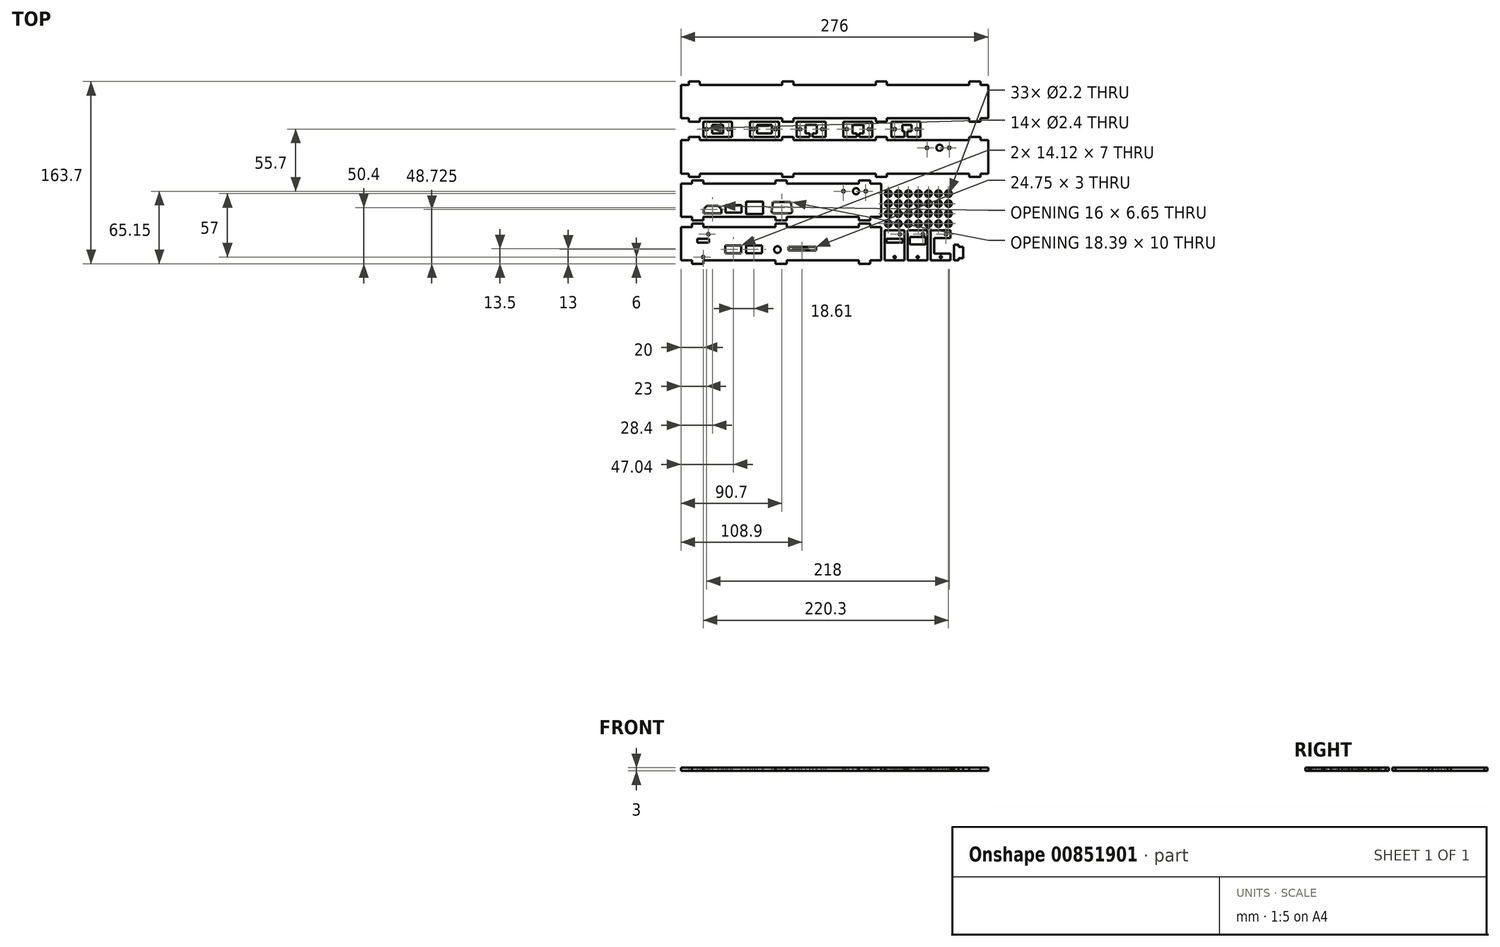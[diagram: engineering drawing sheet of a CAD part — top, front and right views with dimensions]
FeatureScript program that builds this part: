
annotation { "Feature Type Name" : "Feature", "Feature Type Description" : "" }
export const myFeature = defineFeature(function(context is Context, id is Id, definition is map)
    precondition{}
    {
        {
            var Q0;
            Q0=qCreatedBy(makeId("Top.planeOp"),FACE);
            var sketch = newSketch(context, id + "F0", { "sketchPlane" : qUnion([Q0])});
            skLineSegment(sketch, "E0.bottom", {"start": v(0, 0) * mm, "end": v(297, 0) * mm, "construction": true});
            skLineSegment(sketch, "E0.top", {"start": v(0, 210) * mm, "end": v(297, 210) * mm, "construction": true});
            skLineSegment(sketch, "E0.left", {"start": v(0, 0) * mm, "end": v(0, 210) * mm, "construction": true});
            skLineSegment(sketch, "E0.right", {"start": v(297, 0) * mm, "end": v(297, 210) * mm, "construction": true});
            skLineSegment(sketch, "E1.bottom", {"start": v(51, 132.7) * mm, "end": v(25, 132.7) * mm});
            skLineSegment(sketch, "E1.top", {"start": v(51, 119) * mm, "end": v(25, 119) * mm});
            skLineSegment(sketch, "E1.left", {"start": v(51, 132.7) * mm, "end": v(51, 119) * mm});
            skLineSegment(sketch, "E1.right", {"start": v(25, 132.7) * mm, "end": v(25, 119) * mm});
            skCircle(sketch, "E2", {"center": v(28, 125.85) * mm, "radius": 1.2 * mm});
            skCircle(sketch, "E3.MirrorC", {"center": v(48, 125.85) * mm, "radius": 1.2 * mm});
            skLineSegment(sketch, "E4.bottom", {"start": v(43, 129.7) * mm, "end": v(33, 129.7) * mm});
            skLineSegment(sketch, "E4.top", {"start": v(43, 122) * mm, "end": v(33, 122) * mm});
            skLineSegment(sketch, "E4.left", {"start": v(43, 129.7) * mm, "end": v(43, 122) * mm});
            skLineSegment(sketch, "E4.right", {"start": v(33, 129.7) * mm, "end": v(33, 122) * mm});
            skPoint(sketch, "E4.middle", {"position": v(38, 125.85) * mm});
            skLineSegment(sketch, "E5", {"start": v(95, 80) * mm, "end": v(95, 44) * mm, "construction": true});
            skLineSegment(sketch, "E6", {"start": v(143, 135.7) * mm, "end": v(143, 165.7) * mm, "construction": true});
            skLineSegment(sketch, "E7", {"start": v(95, 41) * mm, "end": v(95, 5) * mm, "construction": true});
            skLineSegment(sketch, "E8", {"start": v(25, 125.85) * mm, "end": v(51, 125.85) * mm, "construction": true});
            skLineSegment(sketch, "E9.bottom", {"start": v(93, 132.7) * mm, "end": v(67, 132.7) * mm});
            skLineSegment(sketch, "E9.top", {"start": v(93, 119) * mm, "end": v(67, 119) * mm});
            skLineSegment(sketch, "E9.left", {"start": v(93, 132.7) * mm, "end": v(93, 119) * mm});
            skLineSegment(sketch, "E9.right", {"start": v(67, 132.7) * mm, "end": v(67, 119) * mm});
            skCircle(sketch, "E10", {"center": v(70, 125.85) * mm, "radius": 1.2 * mm});
            skCircle(sketch, "E11.MirrorC", {"center": v(90, 125.85) * mm, "radius": 1.2 * mm});
            skLineSegment(sketch, "E12.bottom", {"start": v(86.65, 129.7) * mm, "end": v(73.35, 129.7) * mm});
            skLineSegment(sketch, "E12.top", {"start": v(86.65, 122) * mm, "end": v(73.35, 122) * mm});
            skLineSegment(sketch, "E12.left", {"start": v(86.65, 129.7) * mm, "end": v(86.65, 122) * mm});
            skLineSegment(sketch, "E12.right", {"start": v(73.35, 129.7) * mm, "end": v(73.35, 122) * mm});
            skPoint(sketch, "E12.middle", {"position": v(80, 125.85) * mm});
            skLineSegment(sketch, "E13", {"start": v(67, 125.85) * mm, "end": v(93, 125.85) * mm, "construction": true});
            skLineSegment(sketch, "E14.bottom", {"start": v(135, 132.7) * mm, "end": v(109, 132.7) * mm});
            skLineSegment(sketch, "E14.top", {"start": v(135, 119) * mm, "end": v(123.2, 119) * mm});
            skLineSegment(sketch, "E14.left", {"start": v(135, 132.7) * mm, "end": v(135, 119) * mm});
            skLineSegment(sketch, "E14.right", {"start": v(109, 132.7) * mm, "end": v(109, 119) * mm});
            skCircle(sketch, "E15", {"center": v(112, 125.85) * mm, "radius": 1.2 * mm});
            skCircle(sketch, "E16.MirrorC", {"center": v(132, 125.85) * mm, "radius": 1.2 * mm});
            skLineSegment(sketch, "E17.bottom", {"start": v(127, 129.7) * mm, "end": v(117, 129.7) * mm});
            skLineSegment(sketch, "E17.top", {"start": v(127, 122) * mm, "end": v(123.2, 122) * mm});
            skLineSegment(sketch, "E17.left", {"start": v(127, 129.7) * mm, "end": v(127, 122) * mm});
            skLineSegment(sketch, "E17.right", {"start": v(117, 129.7) * mm, "end": v(117, 122) * mm});
            skPoint(sketch, "E17.middle", {"position": v(122, 125.85) * mm});
            skLineSegment(sketch, "E18", {"start": v(109, 125.85) * mm, "end": v(135, 125.85) * mm, "construction": true});
            skLineSegment(sketch, "E19.bottom", {"start": v(220, 132.7) * mm, "end": v(194, 132.7) * mm});
            skLineSegment(sketch, "E19.top", {"start": v(220, 119) * mm, "end": v(208.2, 119) * mm});
            skLineSegment(sketch, "E19.left", {"start": v(220, 132.7) * mm, "end": v(220, 119) * mm});
            skLineSegment(sketch, "E19.right", {"start": v(194, 132.7) * mm, "end": v(194, 119) * mm});
            skCircle(sketch, "E20", {"center": v(197, 125.85) * mm, "radius": 1.2 * mm});
            skCircle(sketch, "E21.MirrorC", {"center": v(217, 125.85) * mm, "radius": 1.2 * mm});
            skLineSegment(sketch, "E22.top", {"start": v(212, 123.9) * mm, "end": v(208.2, 123.9) * mm});
            skPoint(sketch, "E22.middle", {"position": v(207, 125.85) * mm});
            skLineSegment(sketch, "E23", {"start": v(194, 125.85) * mm, "end": v(220, 125.85) * mm, "construction": true});
            skLineSegment(sketch, "E24", {"start": v(123.2, 122) * mm, "end": v(123.2, 119) * mm});
            skLineSegment(sketch, "E25", {"start": v(120.8, 122) * mm, "end": v(120.8, 119) * mm});
            skLineSegment(sketch, "E26", {"start": v(120.8, 122) * mm, "end": v(117, 122) * mm});
            skLineSegment(sketch, "E27", {"start": v(120.8, 119) * mm, "end": v(109, 119) * mm});
            skLineSegment(sketch, "E28", {"start": v(208.2, 123.9) * mm, "end": v(208.2, 119) * mm});
            skLineSegment(sketch, "E29", {"start": v(205.8, 123.9) * mm, "end": v(205.8, 119) * mm});
            skLineSegment(sketch, "E30", {"start": v(212, 123.9) * mm, "end": v(212, 129.7) * mm});
            skLineSegment(sketch, "E31", {"start": v(212, 129.7) * mm, "end": v(203.9, 129.7) * mm});
            skLineSegment(sketch, "E32", {"start": v(203.9, 129.7) * mm, "end": v(203.9, 123.9) * mm});
            skLineSegment(sketch, "E33", {"start": v(203.9, 123.9) * mm, "end": v(205.8, 123.9) * mm});
            skLineSegment(sketch, "E34", {"start": v(205.8, 119) * mm, "end": v(194, 119) * mm});
            skCircle(sketch, "E35", {"center": v(162.3, 70.15) * mm, "radius": 2.8 * mm});
            skCircle(sketch, "E36", {"center": v(171, 70.15) * mm, "radius": 1.2 * mm});
            skCircle(sketch, "E37", {"center": v(151, 70.15) * mm, "radius": 1.2 * mm});
            skLineSegment(sketch, "E38.bottom", {"start": v(177, 132.7) * mm, "end": v(151, 132.7) * mm});
            skLineSegment(sketch, "E38.top", {"start": v(177, 119) * mm, "end": v(165.2, 119) * mm});
            skLineSegment(sketch, "E38.left", {"start": v(177, 132.7) * mm, "end": v(177, 119) * mm});
            skLineSegment(sketch, "E38.right", {"start": v(151, 132.7) * mm, "end": v(151, 119) * mm});
            skCircle(sketch, "E39", {"center": v(154, 125.85) * mm, "radius": 1.2 * mm});
            skCircle(sketch, "E40.MirrorC", {"center": v(174, 125.85) * mm, "radius": 1.2 * mm});
            skLineSegment(sketch, "E41.bottom", {"start": v(169, 129.7) * mm, "end": v(159, 129.7) * mm});
            skLineSegment(sketch, "E41.top", {"start": v(169, 122) * mm, "end": v(165.2, 122) * mm});
            skLineSegment(sketch, "E41.left", {"start": v(169, 129.7) * mm, "end": v(169, 122) * mm});
            skLineSegment(sketch, "E41.right", {"start": v(159, 129.7) * mm, "end": v(159, 122) * mm});
            skPoint(sketch, "E41.middle", {"position": v(164, 125.85) * mm});
            skLineSegment(sketch, "E42", {"start": v(151, 125.85) * mm, "end": v(177, 125.85) * mm, "construction": true});
            skLineSegment(sketch, "E43", {"start": v(165.2, 122) * mm, "end": v(165.2, 119) * mm});
            skLineSegment(sketch, "E44", {"start": v(162.8, 122) * mm, "end": v(162.8, 119) * mm});
            skLineSegment(sketch, "E45", {"start": v(162.8, 122) * mm, "end": v(159, 122) * mm});
            skLineSegment(sketch, "E46", {"start": v(162.8, 119) * mm, "end": v(151, 119) * mm});
            skCircle(sketch, "E47", {"center": v(29.7, 31.5) * mm, "radius": 1.1 * mm});
            skCircle(sketch, "E48", {"center": v(25, 11) * mm, "radius": 1.1 * mm});
            skLineSegment(sketch, "E49", {"start": v(30.1, 24.1) * mm, "end": v(30.1, 27.3) * mm});
            skLineSegment(sketch, "E50", {"start": v(30.1, 27.3) * mm, "end": v(19.9, 27.3) * mm});
            skLineSegment(sketch, "E51", {"start": v(19.9, 27.3) * mm, "end": v(19.9, 24.1) * mm});
            skLineSegment(sketch, "E52", {"start": v(19.9, 24.1) * mm, "end": v(30.1, 24.1) * mm});
            skCircle(sketch, "E53", {"center": v(201.7, 31.5) * mm, "radius": 1.1 * mm});
            skCircle(sketch, "E54", {"center": v(197, 11) * mm, "radius": 1 * mm});
            skLineSegment(sketch, "E55", {"start": v(204.25, 24.1) * mm, "end": v(204.25, 27.3) * mm});
            skLineSegment(sketch, "E56", {"start": v(204.25, 27.3) * mm, "end": v(189.75, 27.3) * mm});
            skLineSegment(sketch, "E57", {"start": v(189.75, 27.3) * mm, "end": v(189.75, 24.1) * mm});
            skLineSegment(sketch, "E58", {"start": v(189.75, 24.1) * mm, "end": v(204.25, 24.1) * mm});
            skLineSegment(sketch, "E59", {"start": v(205.7, 8) * mm, "end": v(205.7, 35) * mm});
            skLineSegment(sketch, "E60", {"start": v(205.7, 35) * mm, "end": v(188, 35) * mm});
            skLineSegment(sketch, "E61", {"start": v(188, 35) * mm, "end": v(188, 8) * mm});
            skLineSegment(sketch, "E62", {"start": v(188, 8) * mm, "end": v(205.7, 8) * mm});
            skCircle(sketch, "E63", {"center": v(222.4, 31.5) * mm, "radius": 1.1 * mm});
            skCircle(sketch, "E64", {"center": v(217.7, 11) * mm, "radius": 1 * mm});
            skLineSegment(sketch, "E65", {"start": v(224.95, 22.45) * mm, "end": v(224.95, 28.95) * mm});
            skLineSegment(sketch, "E66", {"start": v(224.95, 28.95) * mm, "end": v(210.45, 28.95) * mm});
            skLineSegment(sketch, "E67", {"start": v(210.45, 28.95) * mm, "end": v(210.45, 22.45) * mm});
            skLineSegment(sketch, "E68", {"start": v(210.45, 22.45) * mm, "end": v(224.95, 22.45) * mm});
            skLineSegment(sketch, "E69", {"start": v(226.4, 8) * mm, "end": v(226.4, 35) * mm});
            skLineSegment(sketch, "E70", {"start": v(226.4, 35) * mm, "end": v(208.7, 35) * mm});
            skLineSegment(sketch, "E71", {"start": v(208.7, 35) * mm, "end": v(208.7, 8) * mm});
            skLineSegment(sketch, "E72", {"start": v(208.7, 8) * mm, "end": v(226.4, 8) * mm});
            skCircle(sketch, "E73", {"center": v(243.1, 31.5) * mm, "radius": 1.1 * mm});
            skCircle(sketch, "E74", {"center": v(238.4, 11) * mm, "radius": 1 * mm});
            skLineSegment(sketch, "E75", {"start": v(247.1, 28) * mm, "end": v(232.4, 28) * mm});
            skLineSegment(sketch, "E76", {"start": v(232.4, 28) * mm, "end": v(232.4, 14) * mm});
            skLineSegment(sketch, "E77", {"start": v(232.4, 14) * mm, "end": v(247.1, 14) * mm});
            skLineSegment(sketch, "E78", {"start": v(247.1, 8) * mm, "end": v(247.1, 14) * mm});
            skLineSegment(sketch, "E79", {"start": v(247.1, 35) * mm, "end": v(229.4, 35) * mm});
            skLineSegment(sketch, "E80", {"start": v(229.4, 35) * mm, "end": v(229.4, 8) * mm});
            skLineSegment(sketch, "E81", {"start": v(229.4, 8) * mm, "end": v(247.1, 8) * mm});
            skLineSegment(sketch, "E82", {"start": v(250.1, 22.2) * mm, "end": v(250.1, 8) * mm});
            skLineSegment(sketch, "E83", {"start": v(250.1, 8) * mm, "end": v(254.5, 8) * mm});
            skLineSegment(sketch, "E84", {"start": v(254.5, 8) * mm, "end": v(254.5, 10.1) * mm});
            skLineSegment(sketch, "E85", {"start": v(254.5, 10.1) * mm, "end": v(258.5, 10.1) * mm});
            skLineSegment(sketch, "E86", {"start": v(258.5, 10.1) * mm, "end": v(258.5, 20.1) * mm});
            skLineSegment(sketch, "E87", {"start": v(258.5, 20.1) * mm, "end": v(254.5, 20.1) * mm});
            skLineSegment(sketch, "E88", {"start": v(254.5, 20.1) * mm, "end": v(254.5, 22.2) * mm});
            skLineSegment(sketch, "E89", {"start": v(254.5, 22.2) * mm, "end": v(250.1, 22.2) * mm});
            skLineSegment(sketch, "E90", {"start": v(95.7, 51.4) * mm, "end": v(95.7, 59.4) * mm, "construction": true});
            skLineSegment(sketch, "E91", {"start": v(103.3, 52) * mm, "end": v(102.5, 58.8) * mm, "construction": true});
            skLineSegment(sketch, "E92.bottom", {"start": v(126.27, 17) * mm, "end": v(101.53, 17) * mm});
            skLineSegment(sketch, "E92.top", {"start": v(126.27, 20) * mm, "end": v(101.53, 20) * mm});
            skLineSegment(sketch, "E92.left", {"start": v(126.27, 17) * mm, "end": v(126.27, 20) * mm});
            skLineSegment(sketch, "E92.right", {"start": v(101.53, 17) * mm, "end": v(101.53, 20) * mm});
            skPoint(sketch, "E92.middle", {"position": v(113.9, 18.5) * mm});
            skCircle(sketch, "E93", {"center": v(91.7, 17.75) * mm, "radius": 2.5 * mm, "construction": true});
            skLineSegment(sketch, "E94.bottom", {"start": v(77.21, 21) * mm, "end": v(64.1, 21) * mm, "construction": true});
            skLineSegment(sketch, "E94.top", {"start": v(77.21, 15) * mm, "end": v(64.1, 15) * mm, "construction": true});
            skLineSegment(sketch, "E94.left", {"start": v(77.21, 21) * mm, "end": v(77.21, 15) * mm, "construction": true});
            skLineSegment(sketch, "E94.right", {"start": v(64.1, 21) * mm, "end": v(64.1, 15) * mm, "construction": true});
            skPoint(sketch, "E94.middle", {"position": v(70.65, 18) * mm});
            skLineSegment(sketch, "E95.bottom", {"start": v(58.6, 15) * mm, "end": v(45.48, 15) * mm, "construction": true});
            skLineSegment(sketch, "E95.top", {"start": v(58.6, 21) * mm, "end": v(45.48, 21) * mm, "construction": true});
            skLineSegment(sketch, "E95.left", {"start": v(58.6, 15) * mm, "end": v(58.6, 21) * mm, "construction": true});
            skLineSegment(sketch, "E95.right", {"start": v(45.48, 15) * mm, "end": v(45.48, 21) * mm, "construction": true});
            skPoint(sketch, "E95.middle", {"position": v(52.04, 18) * mm});
            skLineSegment(sketch, "E96.0", {"start": v(59.1, 21.5) * mm, "end": v(44.98, 21.5) * mm});
            skLineSegment(sketch, "E96.1", {"start": v(59.1, 14.5) * mm, "end": v(59.1, 21.5) * mm});
            skLineSegment(sketch, "E96.2", {"start": v(59.1, 14.5) * mm, "end": v(44.98, 14.5) * mm});
            skLineSegment(sketch, "E96.3", {"start": v(44.98, 14.5) * mm, "end": v(44.98, 21.5) * mm});
            skLineSegment(sketch, "E97.0", {"start": v(77.71, 21.5) * mm, "end": v(63.6, 21.5) * mm});
            skLineSegment(sketch, "E97.1", {"start": v(77.71, 21.5) * mm, "end": v(77.71, 14.5) * mm});
            skLineSegment(sketch, "E97.2", {"start": v(77.71, 14.5) * mm, "end": v(63.6, 14.5) * mm});
            skLineSegment(sketch, "E97.3", {"start": v(63.6, 21.5) * mm, "end": v(63.6, 14.5) * mm});
            skCircle(sketch, "E98.0", {"center": v(91.7, 17.75) * mm, "radius": 3 * mm});
            skCircle(sketch, "E99", {"center": v(237.3, 109.15) * mm, "radius": 2.8 * mm});
            skCircle(sketch, "E100", {"center": v(246, 109.15) * mm, "radius": 1.2 * mm});
            skCircle(sketch, "E101", {"center": v(226, 109.15) * mm, "radius": 1.2 * mm});
            skPoint(sketch, "E102", {"position": v(52.3, 54.3) * mm});
            skPoint(sketch, "E103", {"position": v(71.2, 55.3) * mm});
            skPoint(sketch, "E104", {"position": v(33.4, 53.73) * mm});
            skPoint(sketch, "E105", {"position": v(95.7, 55.4) * mm});
            skLineSegment(sketch, "E106.bottom", {"start": v(78.35, 60.4) * mm, "end": v(64.05, 60.4) * mm, "construction": true});
            skLineSegment(sketch, "E106.top", {"start": v(78.35, 50.2) * mm, "end": v(64.05, 50.2) * mm, "construction": true});
            skLineSegment(sketch, "E106.left", {"start": v(78.35, 60.4) * mm, "end": v(78.35, 50.2) * mm, "construction": true});
            skLineSegment(sketch, "E106.right", {"start": v(64.05, 60.4) * mm, "end": v(64.05, 50.2) * mm, "construction": true});
            skLineSegment(sketch, "E107.0", {"start": v(78.85, 60.9) * mm, "end": v(63.55, 60.9) * mm});
            skLineSegment(sketch, "E107.1", {"start": v(78.85, 60.9) * mm, "end": v(78.85, 49.7) * mm});
            skLineSegment(sketch, "E107.2", {"start": v(78.85, 49.7) * mm, "end": v(63.55, 49.7) * mm});
            skLineSegment(sketch, "E107.3", {"start": v(63.55, 60.9) * mm, "end": v(63.55, 49.7) * mm});
            skLineSegment(sketch, "E108.bottom", {"start": v(58.9, 57.2) * mm, "end": v(45.7, 57.2) * mm, "construction": true});
            skLineSegment(sketch, "E108.top", {"start": v(58.9, 51.4) * mm, "end": v(45.7, 51.4) * mm, "construction": true});
            skLineSegment(sketch, "E108.left", {"start": v(58.9, 57.2) * mm, "end": v(58.9, 51.4) * mm, "construction": true});
            skLineSegment(sketch, "E108.right", {"start": v(45.7, 57.2) * mm, "end": v(45.7, 51.4) * mm, "construction": true});
            skLineSegment(sketch, "E109.0", {"start": v(59.4, 57.7) * mm, "end": v(45.2, 57.7) * mm});
            skLineSegment(sketch, "E109.1", {"start": v(59.4, 57.7) * mm, "end": v(59.4, 50.9) * mm});
            skLineSegment(sketch, "E109.2", {"start": v(59.4, 50.9) * mm, "end": v(45.2, 50.9) * mm});
            skLineSegment(sketch, "E109.3", {"start": v(45.2, 57.7) * mm, "end": v(45.2, 50.9) * mm});
            skLineSegment(sketch, "E110", {"start": v(25.9, 50.9) * mm, "end": v(40.9, 50.9) * mm, "construction": true});
            skLineSegment(sketch, "E111", {"start": v(40.9, 50.9) * mm, "end": v(40.9, 54.05) * mm, "construction": true});
            skLineSegment(sketch, "E112", {"start": v(25.9, 50.9) * mm, "end": v(25.9, 54.05) * mm, "construction": true});
            skLineSegment(sketch, "E113", {"start": v(33.4, 50.9) * mm, "end": v(33.4, 56.55) * mm, "construction": true});
            skLineSegment(sketch, "E114", {"start": v(40.9, 54.05) * mm, "end": v(38.4, 56.55) * mm, "construction": true});
            skLineSegment(sketch, "E115", {"start": v(25.9, 54.05) * mm, "end": v(28.4, 56.55) * mm, "construction": true});
            skLineSegment(sketch, "E116", {"start": v(38.4, 56.55) * mm, "end": v(28.4, 56.55) * mm, "construction": true});
            skLineSegment(sketch, "E117.0", {"start": v(41.4, 54.26) * mm, "end": v(38.6, 57.05) * mm});
            skLineSegment(sketch, "E117.1", {"start": v(25.4, 54.26) * mm, "end": v(28.2, 57.05) * mm});
            skLineSegment(sketch, "E117.2", {"start": v(25.4, 50.4) * mm, "end": v(25.4, 54.26) * mm});
            skLineSegment(sketch, "E117.3", {"start": v(38.6, 57.05) * mm, "end": v(28.2, 57.05) * mm});
            skLineSegment(sketch, "E117.4", {"start": v(25.4, 50.4) * mm, "end": v(41.4, 50.4) * mm});
            skLineSegment(sketch, "E117.5", {"start": v(41.4, 50.4) * mm, "end": v(41.4, 54.26) * mm});
            skLineSegment(sketch, "E118", {"start": v(88.1, 51.4) * mm, "end": v(103.3, 51.4) * mm, "construction": true});
            skLineSegment(sketch, "E119", {"start": v(88.9, 59.4) * mm, "end": v(102.5, 59.4) * mm, "construction": true});
            skLineSegment(sketch, "E120", {"start": v(103.3, 52) * mm, "end": v(103.9, 52.07) * mm, "construction": true});
            skLineSegment(sketch, "E121", {"start": v(102.5, 58.8) * mm, "end": v(103.1, 58.87) * mm, "construction": true});
            skLineSegment(sketch, "E122", {"start": v(103.1, 58.87) * mm, "end": v(103.9, 52.07) * mm, "construction": true});
            skArc(sketch, "E123", {"start": v(102.5, 59.4) * mm, "mid": v(102.9, 59.25) * mm, "end": v(103.1, 58.87) * mm, "construction": true});
            skArc(sketch, "E124", {"start": v(103.3, 51.4) * mm, "mid": v(103.75, 51.6) * mm, "end": v(103.9, 52.07) * mm, "construction": true});
            skArc(sketch, "E125.MirrorCS", {"start": v(88.9, 59.4) * mm, "mid": v(88.5, 59.25) * mm, "end": v(88.3, 58.87) * mm, "construction": true});
            skLineSegment(sketch, "E126.MirrorCS", {"start": v(88.3, 58.87) * mm, "end": v(87.5, 52.07) * mm, "construction": true});
            skArc(sketch, "E127.MirrorCS", {"start": v(88.1, 51.4) * mm, "mid": v(87.65, 51.6) * mm, "end": v(87.5, 52.07) * mm, "construction": true});
            skArc(sketch, "E128.0", {"start": v(88.9, 60.4) * mm, "mid": v(87.84, 60) * mm, "end": v(87.31, 58.99) * mm});
            skLineSegment(sketch, "E128.1", {"start": v(88.9, 60.4) * mm, "end": v(102.5, 60.4) * mm});
            skLineSegment(sketch, "E128.2", {"start": v(87.31, 58.99) * mm, "end": v(86.51, 52.19) * mm});
            skArc(sketch, "E128.3", {"start": v(102.5, 60.4) * mm, "mid": v(103.56, 60) * mm, "end": v(104.09, 58.99) * mm});
            skArc(sketch, "E128.4", {"start": v(88.1, 50.4) * mm, "mid": v(86.9, 50.94) * mm, "end": v(86.51, 52.19) * mm});
            skLineSegment(sketch, "E128.5", {"start": v(88.1, 50.4) * mm, "end": v(103.3, 50.4) * mm});
            skArc(sketch, "E128.6", {"start": v(103.3, 50.4) * mm, "mid": v(104.5, 50.94) * mm, "end": v(104.89, 52.19) * mm});
            skLineSegment(sketch, "E128.7", {"start": v(104.09, 58.99) * mm, "end": v(104.89, 52.19) * mm});
            skPoint(sketch, "E129.startSnap0", {"position": v(143, 101) * mm});
            skLineSegment(sketch, "E130", {"start": v(143, 116) * mm, "end": v(143, 86) * mm, "construction": true});
            skLineSegment(sketch, "E131", {"start": v(5, 101) * mm, "end": v(281, 101) * mm, "construction": true});
            skLineSegment(sketch, "E132", {"start": v(143, 86) * mm, "end": v(180, 86) * mm});
            skLineSegment(sketch, "E133", {"start": v(180, 86) * mm, "end": v(180, 83) * mm});
            skLineSegment(sketch, "E134", {"start": v(180, 83) * mm, "end": v(190, 83) * mm});
            skLineSegment(sketch, "E135", {"start": v(190, 83) * mm, "end": v(190, 86) * mm});
            skLineSegment(sketch, "E136", {"start": v(190, 86) * mm, "end": v(264, 86) * mm});
            skLineSegment(sketch, "E137", {"start": v(264, 86) * mm, "end": v(264, 83) * mm});
            skLineSegment(sketch, "E138", {"start": v(264, 83) * mm, "end": v(274, 83) * mm});
            skLineSegment(sketch, "E139", {"start": v(274, 83) * mm, "end": v(274, 86) * mm});
            skLineSegment(sketch, "E140", {"start": v(274, 86) * mm, "end": v(281, 86) * mm});
            skLineSegment(sketch, "E141", {"start": v(281, 86) * mm, "end": v(281, 101) * mm});
            skLineSegment(sketch, "E142.MirrorCS", {"start": v(190, 116) * mm, "end": v(264, 116) * mm});
            skLineSegment(sketch, "E143.MirrorCS", {"start": v(143, 116) * mm, "end": v(180, 116) * mm});
            skLineSegment(sketch, "E144.MirrorCS", {"start": v(190, 119) * mm, "end": v(190, 116) * mm});
            skLineSegment(sketch, "E145.MirrorCS", {"start": v(281, 116) * mm, "end": v(281, 101) * mm});
            skLineSegment(sketch, "E146.MirrorCS", {"start": v(274, 119) * mm, "end": v(274, 116) * mm});
            skLineSegment(sketch, "E147.MirrorCS", {"start": v(180, 116) * mm, "end": v(180, 119) * mm});
            skLineSegment(sketch, "E148.MirrorCS", {"start": v(264, 119) * mm, "end": v(274, 119) * mm});
            skLineSegment(sketch, "E149.MirrorCS", {"start": v(264, 116) * mm, "end": v(264, 119) * mm});
            skLineSegment(sketch, "E150.MirrorCS", {"start": v(180, 119) * mm, "end": v(190, 119) * mm});
            skLineSegment(sketch, "E151.MirrorCS", {"start": v(274, 116) * mm, "end": v(281, 116) * mm});
            skLineSegment(sketch, "E152.MirrorCS", {"start": v(12, 83) * mm, "end": v(12, 86) * mm});
            skLineSegment(sketch, "E153.MirrorCS", {"start": v(106, 86) * mm, "end": v(106, 83) * mm});
            skLineSegment(sketch, "E154.MirrorCS", {"start": v(22, 86) * mm, "end": v(22, 83) * mm});
            skLineSegment(sketch, "E155.MirrorCS", {"start": v(96, 83) * mm, "end": v(96, 86) * mm});
            skLineSegment(sketch, "E156.MirrorCS", {"start": v(5, 86) * mm, "end": v(5, 101) * mm});
            skLineSegment(sketch, "E157.MirrorCS", {"start": v(96, 86) * mm, "end": v(22, 86) * mm});
            skLineSegment(sketch, "E158.MirrorCS", {"start": v(22, 83) * mm, "end": v(12, 83) * mm});
            skLineSegment(sketch, "E159.MirrorCS", {"start": v(12, 86) * mm, "end": v(5, 86) * mm});
            skLineSegment(sketch, "E160.MirrorCS", {"start": v(106, 83) * mm, "end": v(96, 83) * mm});
            skLineSegment(sketch, "E161.MirrorCS", {"start": v(143, 86) * mm, "end": v(106, 86) * mm});
            skLineSegment(sketch, "E162.MirrorCS", {"start": v(96, 119) * mm, "end": v(96, 116) * mm});
            skLineSegment(sketch, "E163.MirrorCS", {"start": v(22, 116) * mm, "end": v(22, 119) * mm});
            skLineSegment(sketch, "E164.MirrorCS", {"start": v(12, 119) * mm, "end": v(12, 116) * mm});
            skLineSegment(sketch, "E165.MirrorCS", {"start": v(106, 116) * mm, "end": v(106, 119) * mm});
            skLineSegment(sketch, "E166.MirrorCS", {"start": v(5, 116) * mm, "end": v(5, 101) * mm});
            skLineSegment(sketch, "E167.MirrorCS", {"start": v(143, 116) * mm, "end": v(106, 116) * mm});
            skLineSegment(sketch, "E168.MirrorCS", {"start": v(12, 116) * mm, "end": v(5, 116) * mm});
            skLineSegment(sketch, "E169.MirrorCS", {"start": v(96, 116) * mm, "end": v(22, 116) * mm});
            skLineSegment(sketch, "E170.MirrorCS", {"start": v(106, 119) * mm, "end": v(96, 119) * mm});
            skLineSegment(sketch, "E171.MirrorCS", {"start": v(22, 119) * mm, "end": v(12, 119) * mm});
            skLineSegment(sketch, "E172", {"start": v(5, 23) * mm, "end": v(185, 23) * mm, "construction": true});
            skPoint(sketch, "E172.startSnap0", {"position": v(95, 23) * mm});
            skLineSegment(sketch, "E173", {"start": v(95, 5) * mm, "end": v(100, 5) * mm});
            skLineSegment(sketch, "E174", {"start": v(100, 5) * mm, "end": v(100, 8) * mm});
            skLineSegment(sketch, "E175", {"start": v(100, 8) * mm, "end": v(165, 8) * mm});
            skLineSegment(sketch, "E176", {"start": v(165, 8) * mm, "end": v(165, 5) * mm});
            skLineSegment(sketch, "E177", {"start": v(165, 5) * mm, "end": v(175, 5) * mm});
            skLineSegment(sketch, "E178", {"start": v(175, 5) * mm, "end": v(175, 8) * mm});
            skLineSegment(sketch, "E179", {"start": v(175, 8) * mm, "end": v(185, 8) * mm});
            skLineSegment(sketch, "E180", {"start": v(185, 8) * mm, "end": v(185, 23) * mm});
            skLineSegment(sketch, "E181.MirrorCS", {"start": v(165, 38) * mm, "end": v(165, 41) * mm});
            skLineSegment(sketch, "E182.MirrorCS", {"start": v(100, 41) * mm, "end": v(100, 38) * mm});
            skLineSegment(sketch, "E183.MirrorCS", {"start": v(175, 41) * mm, "end": v(175, 38) * mm});
            skLineSegment(sketch, "E184.MirrorCS", {"start": v(100, 38) * mm, "end": v(165, 38) * mm});
            skLineSegment(sketch, "E185.MirrorCS", {"start": v(185, 38) * mm, "end": v(185, 23) * mm});
            skLineSegment(sketch, "E186.MirrorCS", {"start": v(95, 41) * mm, "end": v(100, 41) * mm});
            skLineSegment(sketch, "E187.MirrorCS", {"start": v(165, 41) * mm, "end": v(175, 41) * mm});
            skLineSegment(sketch, "E188.MirrorCS", {"start": v(175, 38) * mm, "end": v(185, 38) * mm});
            skLineSegment(sketch, "E189.MirrorCS", {"start": v(15, 5) * mm, "end": v(15, 8) * mm});
            skLineSegment(sketch, "E190.MirrorCS", {"start": v(25, 8) * mm, "end": v(25, 5) * mm});
            skLineSegment(sketch, "E191.MirrorCS", {"start": v(90, 5) * mm, "end": v(90, 8) * mm});
            skLineSegment(sketch, "E192.MirrorCS", {"start": v(15, 8) * mm, "end": v(5, 8) * mm});
            skLineSegment(sketch, "E193.MirrorCS", {"start": v(95, 5) * mm, "end": v(90, 5) * mm});
            skLineSegment(sketch, "E194.MirrorCS", {"start": v(5, 8) * mm, "end": v(5, 23) * mm});
            skLineSegment(sketch, "E195.MirrorCS", {"start": v(25, 5) * mm, "end": v(15, 5) * mm});
            skLineSegment(sketch, "E196.MirrorCS", {"start": v(90, 8) * mm, "end": v(25, 8) * mm});
            skLineSegment(sketch, "E197.MirrorCS", {"start": v(25, 38) * mm, "end": v(25, 41) * mm});
            skLineSegment(sketch, "E198.MirrorCS", {"start": v(5, 38) * mm, "end": v(5, 23) * mm});
            skLineSegment(sketch, "E199.MirrorCS", {"start": v(15, 41) * mm, "end": v(15, 38) * mm});
            skLineSegment(sketch, "E200.MirrorCS", {"start": v(90, 41) * mm, "end": v(90, 38) * mm});
            skLineSegment(sketch, "E201.MirrorCS", {"start": v(95, 41) * mm, "end": v(90, 41) * mm});
            skLineSegment(sketch, "E202.MirrorCS", {"start": v(15, 38) * mm, "end": v(5, 38) * mm});
            skLineSegment(sketch, "E203.MirrorCS", {"start": v(25, 41) * mm, "end": v(15, 41) * mm});
            skLineSegment(sketch, "E204.MirrorCS", {"start": v(90, 38) * mm, "end": v(25, 38) * mm});
            skLineSegment(sketch, "E205", {"start": v(5, 62) * mm, "end": v(185, 62) * mm, "construction": true});
            skPoint(sketch, "E205.startSnap0", {"position": v(95, 62) * mm});
            skLineSegment(sketch, "E206", {"start": v(95, 44) * mm, "end": v(100, 44) * mm});
            skLineSegment(sketch, "E207", {"start": v(100, 44) * mm, "end": v(100, 47) * mm});
            skLineSegment(sketch, "E208", {"start": v(100, 47) * mm, "end": v(165, 47) * mm});
            skLineSegment(sketch, "E209", {"start": v(165, 47) * mm, "end": v(165, 44) * mm});
            skLineSegment(sketch, "E210", {"start": v(165, 44) * mm, "end": v(175, 44) * mm});
            skLineSegment(sketch, "E211", {"start": v(175, 44) * mm, "end": v(175, 47) * mm});
            skLineSegment(sketch, "E212", {"start": v(175, 47) * mm, "end": v(185, 47) * mm});
            skLineSegment(sketch, "E213", {"start": v(185, 47) * mm, "end": v(185, 62) * mm});
            skLineSegment(sketch, "E214.MirrorCS", {"start": v(185, 77) * mm, "end": v(185, 62) * mm});
            skLineSegment(sketch, "E215.MirrorCS", {"start": v(175, 80) * mm, "end": v(175, 77) * mm});
            skLineSegment(sketch, "E216.MirrorCS", {"start": v(165, 80) * mm, "end": v(175, 80) * mm});
            skLineSegment(sketch, "E217.MirrorCS", {"start": v(100, 77) * mm, "end": v(165, 77) * mm});
            skLineSegment(sketch, "E218.MirrorCS", {"start": v(95, 80) * mm, "end": v(100, 80) * mm});
            skLineSegment(sketch, "E219.MirrorCS", {"start": v(165, 77) * mm, "end": v(165, 80) * mm});
            skLineSegment(sketch, "E220.MirrorCS", {"start": v(100, 80) * mm, "end": v(100, 77) * mm});
            skLineSegment(sketch, "E221.MirrorCS", {"start": v(175, 77) * mm, "end": v(185, 77) * mm});
            skLineSegment(sketch, "E222.MirrorCS", {"start": v(5, 47) * mm, "end": v(5, 62) * mm});
            skLineSegment(sketch, "E223.MirrorCS", {"start": v(15, 47) * mm, "end": v(5, 47) * mm});
            skLineSegment(sketch, "E224.MirrorCS", {"start": v(90, 44) * mm, "end": v(90, 47) * mm});
            skLineSegment(sketch, "E225.MirrorCS", {"start": v(25, 47) * mm, "end": v(25, 44) * mm});
            skLineSegment(sketch, "E226.MirrorCS", {"start": v(90, 47) * mm, "end": v(25, 47) * mm});
            skLineSegment(sketch, "E227.MirrorCS", {"start": v(15, 44) * mm, "end": v(15, 47) * mm});
            skLineSegment(sketch, "E228.MirrorCS", {"start": v(25, 44) * mm, "end": v(15, 44) * mm});
            skLineSegment(sketch, "E229.MirrorCS", {"start": v(95, 44) * mm, "end": v(90, 44) * mm});
            skLineSegment(sketch, "E230.MirrorCS", {"start": v(5, 77) * mm, "end": v(5, 62) * mm});
            skLineSegment(sketch, "E231.MirrorCS", {"start": v(95, 80) * mm, "end": v(90, 80) * mm});
            skLineSegment(sketch, "E232.MirrorCS", {"start": v(25, 80) * mm, "end": v(15, 80) * mm});
            skLineSegment(sketch, "E233.MirrorCS", {"start": v(90, 80) * mm, "end": v(90, 77) * mm});
            skLineSegment(sketch, "E234.MirrorCS", {"start": v(15, 80) * mm, "end": v(15, 77) * mm});
            skLineSegment(sketch, "E235.MirrorCS", {"start": v(15, 77) * mm, "end": v(5, 77) * mm});
            skLineSegment(sketch, "E236.MirrorCS", {"start": v(90, 77) * mm, "end": v(25, 77) * mm});
            skLineSegment(sketch, "E237.MirrorCS", {"start": v(25, 77) * mm, "end": v(25, 80) * mm});
            skLineSegment(sketch, "E238", {"start": v(5, 150.7) * mm, "end": v(281, 150.7) * mm, "construction": true});
            skPoint(sketch, "E238.startSnap0", {"position": v(143, 150.7) * mm});
            skLineSegment(sketch, "E239", {"start": v(143, 135.7) * mm, "end": v(180, 135.7) * mm});
            skLineSegment(sketch, "E240", {"start": v(180, 135.7) * mm, "end": v(180, 132.7) * mm});
            skLineSegment(sketch, "E241", {"start": v(180, 132.7) * mm, "end": v(190, 132.7) * mm});
            skLineSegment(sketch, "E242", {"start": v(190, 132.7) * mm, "end": v(190, 135.7) * mm});
            skLineSegment(sketch, "E243", {"start": v(190, 135.7) * mm, "end": v(264, 135.7) * mm});
            skLineSegment(sketch, "E244", {"start": v(264, 135.7) * mm, "end": v(264, 132.7) * mm});
            skLineSegment(sketch, "E245", {"start": v(264, 132.7) * mm, "end": v(274, 132.7) * mm});
            skLineSegment(sketch, "E246", {"start": v(274, 132.7) * mm, "end": v(274, 135.7) * mm});
            skLineSegment(sketch, "E247", {"start": v(274, 135.7) * mm, "end": v(281, 135.7) * mm});
            skLineSegment(sketch, "E248", {"start": v(281, 135.7) * mm, "end": v(281, 150.7) * mm});
            skLineSegment(sketch, "E249.MirrorCS", {"start": v(264, 165.7) * mm, "end": v(264, 168.7) * mm});
            skLineSegment(sketch, "E250.MirrorCS", {"start": v(190, 168.7) * mm, "end": v(190, 165.7) * mm});
            skLineSegment(sketch, "E251.MirrorCS", {"start": v(180, 165.7) * mm, "end": v(180, 168.7) * mm});
            skLineSegment(sketch, "E252.MirrorCS", {"start": v(274, 168.7) * mm, "end": v(274, 165.7) * mm});
            skLineSegment(sketch, "E253.MirrorCS", {"start": v(274, 165.7) * mm, "end": v(281, 165.7) * mm});
            skLineSegment(sketch, "E254.MirrorCS", {"start": v(190, 165.7) * mm, "end": v(264, 165.7) * mm});
            skLineSegment(sketch, "E255.MirrorCS", {"start": v(281, 165.7) * mm, "end": v(281, 150.7) * mm});
            skLineSegment(sketch, "E256.MirrorCS", {"start": v(143, 165.7) * mm, "end": v(180, 165.7) * mm});
            skLineSegment(sketch, "E257.MirrorCS", {"start": v(180, 168.7) * mm, "end": v(190, 168.7) * mm});
            skLineSegment(sketch, "E258.MirrorCS", {"start": v(264, 168.7) * mm, "end": v(274, 168.7) * mm});
            skLineSegment(sketch, "E259.MirrorCS", {"start": v(106, 135.7) * mm, "end": v(106, 132.7) * mm});
            skLineSegment(sketch, "E260.MirrorCS", {"start": v(96, 132.7) * mm, "end": v(96, 135.7) * mm});
            skLineSegment(sketch, "E261.MirrorCS", {"start": v(22, 135.7) * mm, "end": v(22, 132.7) * mm});
            skLineSegment(sketch, "E262.MirrorCS", {"start": v(12, 132.7) * mm, "end": v(12, 135.7) * mm});
            skLineSegment(sketch, "E263.MirrorCS", {"start": v(143, 135.7) * mm, "end": v(106, 135.7) * mm});
            skLineSegment(sketch, "E264.MirrorCS", {"start": v(12, 135.7) * mm, "end": v(5, 135.7) * mm});
            skLineSegment(sketch, "E265.MirrorCS", {"start": v(96, 135.7) * mm, "end": v(22, 135.7) * mm});
            skLineSegment(sketch, "E266.MirrorCS", {"start": v(5, 135.7) * mm, "end": v(5, 150.7) * mm});
            skLineSegment(sketch, "E267.MirrorCS", {"start": v(106, 132.7) * mm, "end": v(96, 132.7) * mm});
            skLineSegment(sketch, "E268.MirrorCS", {"start": v(22, 132.7) * mm, "end": v(12, 132.7) * mm});
            skLineSegment(sketch, "E269.MirrorCS", {"start": v(22, 165.7) * mm, "end": v(22, 168.7) * mm});
            skLineSegment(sketch, "E270.MirrorCS", {"start": v(106, 165.7) * mm, "end": v(106, 168.7) * mm});
            skLineSegment(sketch, "E271.MirrorCS", {"start": v(12, 168.7) * mm, "end": v(12, 165.7) * mm});
            skLineSegment(sketch, "E272.MirrorCS", {"start": v(96, 168.7) * mm, "end": v(96, 165.7) * mm});
            skLineSegment(sketch, "E273.MirrorCS", {"start": v(22, 168.7) * mm, "end": v(12, 168.7) * mm});
            skLineSegment(sketch, "E274.MirrorCS", {"start": v(106, 168.7) * mm, "end": v(96, 168.7) * mm});
            skLineSegment(sketch, "E275.MirrorCS", {"start": v(143, 165.7) * mm, "end": v(106, 165.7) * mm});
            skLineSegment(sketch, "E276.MirrorCS", {"start": v(96, 165.7) * mm, "end": v(22, 165.7) * mm});
            skLineSegment(sketch, "E277.MirrorCS", {"start": v(5, 165.7) * mm, "end": v(5, 150.7) * mm});
            skLineSegment(sketch, "E278.MirrorCS", {"start": v(12, 165.7) * mm, "end": v(5, 165.7) * mm});
            skCircle(sketch, "E279", {"center": v(191.3, 41) * mm, "radius": 1.1 * mm});
            skCircle(sketch, "E280", {"center": v(191.3, 41) * mm, "radius": 3 * mm});
            skCircle(sketch, "E281.0.1.0", {"center": v(191.3, 50) * mm, "radius": 3 * mm});
            skCircle(sketch, "E281.0.1.1", {"center": v(191.3, 50) * mm, "radius": 1.1 * mm});
            skCircle(sketch, "E281.0.2.0", {"center": v(191.3, 59) * mm, "radius": 3 * mm});
            skCircle(sketch, "E281.0.2.1", {"center": v(191.3, 59) * mm, "radius": 1.1 * mm});
            skCircle(sketch, "E281.0.3.0", {"center": v(191.3, 68) * mm, "radius": 3 * mm});
            skCircle(sketch, "E281.0.3.1", {"center": v(191.3, 68) * mm, "radius": 1.1 * mm});
            skCircle(sketch, "E281.1.0.0", {"center": v(200.3, 41) * mm, "radius": 3 * mm});
            skCircle(sketch, "E281.1.0.1", {"center": v(200.3, 41) * mm, "radius": 1.1 * mm});
            skCircle(sketch, "E281.1.1.0", {"center": v(200.3, 50) * mm, "radius": 3 * mm});
            skCircle(sketch, "E281.1.1.1", {"center": v(200.3, 50) * mm, "radius": 1.1 * mm});
            skCircle(sketch, "E281.1.2.0", {"center": v(200.3, 59) * mm, "radius": 3 * mm});
            skCircle(sketch, "E281.1.2.1", {"center": v(200.3, 59) * mm, "radius": 1.1 * mm});
            skCircle(sketch, "E281.1.3.0", {"center": v(200.3, 68) * mm, "radius": 3 * mm});
            skCircle(sketch, "E281.1.3.1", {"center": v(200.3, 68) * mm, "radius": 1.1 * mm});
            skCircle(sketch, "E281.2.0.0", {"center": v(209.3, 41) * mm, "radius": 3 * mm});
            skCircle(sketch, "E281.2.0.1", {"center": v(209.3, 41) * mm, "radius": 1.1 * mm});
            skCircle(sketch, "E281.2.1.0", {"center": v(209.3, 50) * mm, "radius": 3 * mm});
            skCircle(sketch, "E281.2.1.1", {"center": v(209.3, 50) * mm, "radius": 1.1 * mm});
            skCircle(sketch, "E281.2.2.0", {"center": v(209.3, 59) * mm, "radius": 3 * mm});
            skCircle(sketch, "E281.2.2.1", {"center": v(209.3, 59) * mm, "radius": 1.1 * mm});
            skCircle(sketch, "E281.2.3.0", {"center": v(209.3, 68) * mm, "radius": 3 * mm});
            skCircle(sketch, "E281.2.3.1", {"center": v(209.3, 68) * mm, "radius": 1.1 * mm});
            skCircle(sketch, "E281.3.0.0", {"center": v(218.3, 41) * mm, "radius": 3 * mm});
            skCircle(sketch, "E281.3.0.1", {"center": v(218.3, 41) * mm, "radius": 1.1 * mm});
            skCircle(sketch, "E281.3.1.0", {"center": v(218.3, 50) * mm, "radius": 3 * mm});
            skCircle(sketch, "E281.3.1.1", {"center": v(218.3, 50) * mm, "radius": 1.1 * mm});
            skCircle(sketch, "E281.3.2.0", {"center": v(218.3, 59) * mm, "radius": 3 * mm});
            skCircle(sketch, "E281.3.2.1", {"center": v(218.3, 59) * mm, "radius": 1.1 * mm});
            skCircle(sketch, "E281.3.3.0", {"center": v(218.3, 68) * mm, "radius": 3 * mm});
            skCircle(sketch, "E281.3.3.1", {"center": v(218.3, 68) * mm, "radius": 1.1 * mm});
            skCircle(sketch, "E281.4.0.0", {"center": v(227.3, 41) * mm, "radius": 3 * mm});
            skCircle(sketch, "E281.4.0.1", {"center": v(227.3, 41) * mm, "radius": 1.1 * mm});
            skCircle(sketch, "E281.4.1.0", {"center": v(227.3, 50) * mm, "radius": 3 * mm});
            skCircle(sketch, "E281.4.1.1", {"center": v(227.3, 50) * mm, "radius": 1.1 * mm});
            skCircle(sketch, "E281.4.2.0", {"center": v(227.3, 59) * mm, "radius": 3 * mm});
            skCircle(sketch, "E281.4.2.1", {"center": v(227.3, 59) * mm, "radius": 1.1 * mm});
            skCircle(sketch, "E281.4.3.0", {"center": v(227.3, 68) * mm, "radius": 3 * mm});
            skCircle(sketch, "E281.4.3.1", {"center": v(227.3, 68) * mm, "radius": 1.1 * mm});
            skCircle(sketch, "E281.5.0.0", {"center": v(236.3, 41) * mm, "radius": 3 * mm});
            skCircle(sketch, "E281.5.0.1", {"center": v(236.3, 41) * mm, "radius": 1.1 * mm});
            skCircle(sketch, "E281.5.1.0", {"center": v(236.3, 50) * mm, "radius": 3 * mm});
            skCircle(sketch, "E281.5.1.1", {"center": v(236.3, 50) * mm, "radius": 1.1 * mm});
            skCircle(sketch, "E281.5.2.0", {"center": v(236.3, 59) * mm, "radius": 3 * mm});
            skCircle(sketch, "E281.5.2.1", {"center": v(236.3, 59) * mm, "radius": 1.1 * mm});
            skCircle(sketch, "E281.5.3.0", {"center": v(236.3, 68) * mm, "radius": 3 * mm});
            skCircle(sketch, "E281.5.3.1", {"center": v(236.3, 68) * mm, "radius": 1.1 * mm});
            skCircle(sketch, "E281.6.0.0", {"center": v(245.3, 41) * mm, "radius": 3 * mm});
            skCircle(sketch, "E281.6.0.1", {"center": v(245.3, 41) * mm, "radius": 1.1 * mm});
            skCircle(sketch, "E281.6.1.0", {"center": v(245.3, 50) * mm, "radius": 3 * mm});
            skCircle(sketch, "E281.6.1.1", {"center": v(245.3, 50) * mm, "radius": 1.1 * mm});
            skCircle(sketch, "E281.6.2.0", {"center": v(245.3, 59) * mm, "radius": 3 * mm});
            skCircle(sketch, "E281.6.2.1", {"center": v(245.3, 59) * mm, "radius": 1.1 * mm});
            skCircle(sketch, "E281.6.3.0", {"center": v(245.3, 68) * mm, "radius": 3 * mm});
            skCircle(sketch, "E281.6.3.1", {"center": v(245.3, 68) * mm, "radius": 1.1 * mm});
            skLineSegment(sketch, "E281.direction1", {"start": v(191.3, 41) * mm, "end": v(200.3, 41) * mm, "construction": true});
            skLineSegment(sketch, "E281.direction2", {"start": v(191.3, 41) * mm, "end": v(191.3, 50) * mm, "construction": true});
            skCircle(sketch, "E282.0.0.4", {"center": v(191.3, 77) * mm, "radius": 3 * mm});
            skCircle(sketch, "E282.2.0.4", {"center": v(191.3, 77) * mm, "radius": 1.1 * mm});
            skCircle(sketch, "E282.0.1.4", {"center": v(200.3, 77) * mm, "radius": 3 * mm});
            skCircle(sketch, "E282.2.1.4", {"center": v(200.3, 77) * mm, "radius": 1.1 * mm});
            skCircle(sketch, "E282.0.2.4", {"center": v(209.3, 77) * mm, "radius": 3 * mm});
            skCircle(sketch, "E282.2.2.4", {"center": v(209.3, 77) * mm, "radius": 1.1 * mm});
            skCircle(sketch, "E282.0.3.4", {"center": v(218.3, 77) * mm, "radius": 3 * mm});
            skCircle(sketch, "E282.2.3.4", {"center": v(218.3, 77) * mm, "radius": 1.1 * mm});
            skCircle(sketch, "E282.0.4.4", {"center": v(227.3, 77) * mm, "radius": 3 * mm});
            skCircle(sketch, "E282.2.4.4", {"center": v(227.3, 77) * mm, "radius": 1.1 * mm});
            skCircle(sketch, "E282.0.5.4", {"center": v(236.3, 77) * mm, "radius": 3 * mm});
            skCircle(sketch, "E282.2.5.4", {"center": v(236.3, 77) * mm, "radius": 1.1 * mm});
            skCircle(sketch, "E282.0.6.4", {"center": v(245.3, 77) * mm, "radius": 3 * mm});
            skCircle(sketch, "E282.2.6.4", {"center": v(245.3, 77) * mm, "radius": 1.1 * mm});
            skLineSegment(sketch, "E283", {"start": v(247.1, 28) * mm, "end": v(247.1, 35) * mm});
            skSolve(sketch);
        }
        {
            var Q0;
            Q0=makeQuery(id+"F0.imprint","IMPRINT",FACE,{"disambiguationData":[TD([[makeQuery(id+"F0.imprint","IMPRINT",EDGE,{"derivedFrom":sQuery(id+"F0.wireOp",EDGE,"E47")}),-1.0]])]});
            extrude(context, id + "F1", {"entities" : qUnion([Q0]), "depth" : 3 * mm, "offsetDistance" : 25 * mm});
        }
        {
            var Q0;
            Q0=makeQuery(id+"F0.imprint","IMPRINT",FACE,{"disambiguationData":[TD([[makeQuery(id+"F0.imprint","IMPRINT",EDGE,{"derivedFrom":sQuery(id+"F0.wireOp",EDGE,"E35")}),-1.0]])]});
            extrude(context, id + "F2", {"entities" : qUnion([Q0]), "depth" : 3 * mm, "offsetDistance" : 25 * mm});
        }
        {
            var Q0;
            Q0=makeQuery(id+"F0.imprint","IMPRINT",FACE,{"disambiguationData":[TD([[makeQuery(id+"F0.imprint","IMPRINT",EDGE,{"derivedFrom":sQuery(id+"F0.wireOp",EDGE,"E99")}),-1.0]])]});
            extrude(context, id + "F3", {"entities" : qUnion([Q0]), "depth" : 3 * mm, "offsetDistance" : 25 * mm});
        }
        {
            var Q0;
            Q0=makeQuery(id+"F0.imprint","IMPRINT",FACE,{"disambiguationData":[TD([[makeQuery(id+"F0.imprint","IMPRINT",EDGE,{"derivedFrom":sQuery(id+"F0.wireOp",EDGE,"E239")}),1.0]])]});
            extrude(context, id + "F4", {"entities" : qUnion([Q0]), "depth" : 3 * mm, "offsetDistance" : 25 * mm});
        }
        {
            var Q0;
            Q0=makeQuery(id+"F0.imprint","IMPRINT",FACE,{"disambiguationData":[TD([[makeQuery(id+"F0.imprint","IMPRINT",EDGE,{"derivedFrom":sQuery(id+"F0.wireOp",EDGE,"E1.bottom")}),1.0]])]});
            extrude(context, id + "F5", {"entities" : qUnion([Q0]), "depth" : 3 * mm, "offsetDistance" : 25 * mm});
        }
        {
            var Q0;
            Q0=makeQuery(id+"F0.imprint","IMPRINT",FACE,{"disambiguationData":[TD([[makeQuery(id+"F0.imprint","IMPRINT",EDGE,{"derivedFrom":sQuery(id+"F0.wireOp",EDGE,"E9.bottom")}),1.0]])]});
            extrude(context, id + "F6", {"entities" : qUnion([Q0]), "depth" : 3 * mm, "offsetDistance" : 25 * mm});
        }
        {
            var Q0;
            Q0=makeQuery(id+"F0.imprint","IMPRINT",FACE,{"disambiguationData":[TD([[makeQuery(id+"F0.imprint","IMPRINT",EDGE,{"derivedFrom":sQuery(id+"F0.wireOp",EDGE,"E14.bottom")}),1.0]])]});
            extrude(context, id + "F7", {"entities" : qUnion([Q0]), "depth" : 3 * mm, "offsetDistance" : 25 * mm});
        }
        {
            var Q0;
            Q0=makeQuery(id+"F0.imprint","IMPRINT",FACE,{"disambiguationData":[TD([[makeQuery(id+"F0.imprint","IMPRINT",EDGE,{"derivedFrom":sQuery(id+"F0.wireOp",EDGE,"E38.bottom")}),1.0]])]});
            extrude(context, id + "F8", {"entities" : qUnion([Q0]), "depth" : 3 * mm, "offsetDistance" : 25 * mm});
        }
        {
            var Q0;
            Q0=makeQuery(id+"F0.imprint","IMPRINT",FACE,{"disambiguationData":[TD([[makeQuery(id+"F0.imprint","IMPRINT",EDGE,{"derivedFrom":sQuery(id+"F0.wireOp",EDGE,"E19.bottom")}),1.0]])]});
            extrude(context, id + "F9", {"entities" : qUnion([Q0]), "depth" : 3 * mm, "offsetDistance" : 25 * mm});
        }
        {
            var Q0;
            Q0=makeQuery(id+"F0.imprint","IMPRINT",FACE,{"disambiguationData":[TD([[makeQuery(id+"F0.imprint","IMPRINT",EDGE,{"derivedFrom":sQuery(id+"F0.wireOp",EDGE,"E53")}),-1.0]])]});
            extrude(context, id + "F10", {"entities" : qUnion([Q0]), "depth" : 3 * mm, "offsetDistance" : 25 * mm});
        }
        {
            var Q0;
            Q0=makeQuery(id+"F0.imprint","IMPRINT",FACE,{"disambiguationData":[TD([[makeQuery(id+"F0.imprint","IMPRINT",EDGE,{"derivedFrom":sQuery(id+"F0.wireOp",EDGE,"E63")}),-1.0]])]});
            extrude(context, id + "F11", {"entities" : qUnion([Q0]), "depth" : 3 * mm, "offsetDistance" : 25 * mm});
        }
        {
            var Q0;
            Q0=makeQuery(id+"F0.imprint","IMPRINT",FACE,{"disambiguationData":[TD([[makeQuery(id+"F0.imprint","IMPRINT",EDGE,{"derivedFrom":sQuery(id+"F0.wireOp",EDGE,"E73")}),-1.0]])]});
            extrude(context, id + "F12", {"entities" : qUnion([Q0]), "depth" : 3 * mm, "offsetDistance" : 25 * mm});
        }
        {
            var Q0;
            Q0=makeQuery(id+"F0.imprint","IMPRINT",FACE,{"disambiguationData":[TD([[makeQuery(id+"F0.imprint","IMPRINT",EDGE,{"derivedFrom":sQuery(id+"F0.wireOp",EDGE,"E82")}),1.0]])]});
            extrude(context, id + "F13", {"entities" : qUnion([Q0]), "depth" : 3 * mm, "offsetDistance" : 25 * mm});
        }
        {
            var Q0;
            Q0=makeQuery(id+"F0.imprint","IMPRINT",FACE,{"disambiguationData":[TD([[makeQuery(id+"F0.imprint","IMPRINT",EDGE,{"derivedFrom":sQuery(id+"F0.wireOp",EDGE,"E279")}),-1.0]])]});
            extrude(context, id + "F14", {"entities" : qUnion([Q0]), "depth" : 3 * mm, "offsetDistance" : 25 * mm});
        }
        {
            var Q0;
            Q0=makeQuery(id+"F0.imprint","IMPRINT",FACE,{"disambiguationData":[TD([[makeQuery(id+"F0.imprint","IMPRINT",EDGE,{"derivedFrom":sQuery(id+"F0.wireOp",EDGE,"E281.1.0.0")}),1.0]])]});
            var Q1;
            Q1=makeQuery(id+"F0.imprint","IMPRINT",FACE,{"disambiguationData":[TD([[makeQuery(id+"F0.imprint","IMPRINT",EDGE,{"derivedFrom":sQuery(id+"F0.wireOp",EDGE,"E281.2.0.0")}),1.0]])]});
            var Q2;
            Q2=makeQuery(id+"F0.imprint","IMPRINT",FACE,{"disambiguationData":[TD([[makeQuery(id+"F0.imprint","IMPRINT",EDGE,{"derivedFrom":sQuery(id+"F0.wireOp",EDGE,"E281.3.0.0")}),1.0]])]});
            var Q3;
            Q3=makeQuery(id+"F0.imprint","IMPRINT",FACE,{"disambiguationData":[TD([[makeQuery(id+"F0.imprint","IMPRINT",EDGE,{"derivedFrom":sQuery(id+"F0.wireOp",EDGE,"E281.4.0.0")}),1.0]])]});
            var Q4;
            Q4=makeQuery(id+"F0.imprint","IMPRINT",FACE,{"disambiguationData":[TD([[makeQuery(id+"F0.imprint","IMPRINT",EDGE,{"derivedFrom":sQuery(id+"F0.wireOp",EDGE,"E281.5.0.0")}),1.0]])]});
            var Q5;
            Q5=makeQuery(id+"F0.imprint","IMPRINT",FACE,{"disambiguationData":[TD([[makeQuery(id+"F0.imprint","IMPRINT",EDGE,{"derivedFrom":sQuery(id+"F0.wireOp",EDGE,"E281.6.0.0")}),1.0]])]});
            var Q6;
            Q6=makeQuery(id+"F0.imprint","IMPRINT",FACE,{"disambiguationData":[TD([[makeQuery(id+"F0.imprint","IMPRINT",EDGE,{"derivedFrom":sQuery(id+"F0.wireOp",EDGE,"E281.6.1.0")}),1.0]])]});
            var Q7;
            Q7=makeQuery(id+"F0.imprint","IMPRINT",FACE,{"disambiguationData":[TD([[makeQuery(id+"F0.imprint","IMPRINT",EDGE,{"derivedFrom":sQuery(id+"F0.wireOp",EDGE,"E281.5.1.0")}),1.0]])]});
            var Q8;
            Q8=makeQuery(id+"F0.imprint","IMPRINT",FACE,{"disambiguationData":[TD([[makeQuery(id+"F0.imprint","IMPRINT",EDGE,{"derivedFrom":sQuery(id+"F0.wireOp",EDGE,"E281.4.1.0")}),1.0]])]});
            var Q9;
            Q9=makeQuery(id+"F0.imprint","IMPRINT",FACE,{"disambiguationData":[TD([[makeQuery(id+"F0.imprint","IMPRINT",EDGE,{"derivedFrom":sQuery(id+"F0.wireOp",EDGE,"E281.3.1.0")}),1.0]])]});
            var Q10;
            Q10=makeQuery(id+"F0.imprint","IMPRINT",FACE,{"disambiguationData":[TD([[makeQuery(id+"F0.imprint","IMPRINT",EDGE,{"derivedFrom":sQuery(id+"F0.wireOp",EDGE,"E281.2.1.0")}),1.0]])]});
            var Q11;
            Q11=makeQuery(id+"F0.imprint","IMPRINT",FACE,{"disambiguationData":[TD([[makeQuery(id+"F0.imprint","IMPRINT",EDGE,{"derivedFrom":sQuery(id+"F0.wireOp",EDGE,"E281.1.1.0")}),1.0]])]});
            var Q12;
            Q12=makeQuery(id+"F0.imprint","IMPRINT",FACE,{"disambiguationData":[TD([[makeQuery(id+"F0.imprint","IMPRINT",EDGE,{"derivedFrom":sQuery(id+"F0.wireOp",EDGE,"E281.0.1.0")}),1.0]])]});
            var Q13;
            Q13=makeQuery(id+"F0.imprint","IMPRINT",FACE,{"disambiguationData":[TD([[makeQuery(id+"F0.imprint","IMPRINT",EDGE,{"derivedFrom":sQuery(id+"F0.wireOp",EDGE,"E281.0.2.0")}),1.0]])]});
            var Q14;
            Q14=makeQuery(id+"F0.imprint","IMPRINT",FACE,{"disambiguationData":[TD([[makeQuery(id+"F0.imprint","IMPRINT",EDGE,{"derivedFrom":sQuery(id+"F0.wireOp",EDGE,"E281.1.2.0")}),1.0]])]});
            var Q15;
            Q15=makeQuery(id+"F0.imprint","IMPRINT",FACE,{"disambiguationData":[TD([[makeQuery(id+"F0.imprint","IMPRINT",EDGE,{"derivedFrom":sQuery(id+"F0.wireOp",EDGE,"E281.2.2.0")}),1.0]])]});
            var Q16;
            Q16=makeQuery(id+"F0.imprint","IMPRINT",FACE,{"disambiguationData":[TD([[makeQuery(id+"F0.imprint","IMPRINT",EDGE,{"derivedFrom":sQuery(id+"F0.wireOp",EDGE,"E281.3.2.0")}),1.0]])]});
            var Q17;
            Q17=makeQuery(id+"F0.imprint","IMPRINT",FACE,{"disambiguationData":[TD([[makeQuery(id+"F0.imprint","IMPRINT",EDGE,{"derivedFrom":sQuery(id+"F0.wireOp",EDGE,"E281.4.2.0")}),1.0]])]});
            var Q18;
            Q18=makeQuery(id+"F0.imprint","IMPRINT",FACE,{"disambiguationData":[TD([[makeQuery(id+"F0.imprint","IMPRINT",EDGE,{"derivedFrom":sQuery(id+"F0.wireOp",EDGE,"E281.5.2.0")}),1.0]])]});
            var Q19;
            Q19=makeQuery(id+"F0.imprint","IMPRINT",FACE,{"disambiguationData":[TD([[makeQuery(id+"F0.imprint","IMPRINT",EDGE,{"derivedFrom":sQuery(id+"F0.wireOp",EDGE,"E281.6.2.0")}),1.0]])]});
            var Q20;
            Q20=makeQuery(id+"F0.imprint","IMPRINT",FACE,{"disambiguationData":[TD([[makeQuery(id+"F0.imprint","IMPRINT",EDGE,{"derivedFrom":sQuery(id+"F0.wireOp",EDGE,"E281.6.3.0")}),1.0]])]});
            var Q21;
            Q21=makeQuery(id+"F0.imprint","IMPRINT",FACE,{"disambiguationData":[TD([[makeQuery(id+"F0.imprint","IMPRINT",EDGE,{"derivedFrom":sQuery(id+"F0.wireOp",EDGE,"E281.5.3.0")}),1.0]])]});
            var Q22;
            Q22=makeQuery(id+"F0.imprint","IMPRINT",FACE,{"disambiguationData":[TD([[makeQuery(id+"F0.imprint","IMPRINT",EDGE,{"derivedFrom":sQuery(id+"F0.wireOp",EDGE,"E281.4.3.0")}),1.0]])]});
            var Q23;
            Q23=makeQuery(id+"F0.imprint","IMPRINT",FACE,{"disambiguationData":[TD([[makeQuery(id+"F0.imprint","IMPRINT",EDGE,{"derivedFrom":sQuery(id+"F0.wireOp",EDGE,"E281.3.3.0")}),1.0]])]});
            var Q24;
            Q24=makeQuery(id+"F0.imprint","IMPRINT",FACE,{"disambiguationData":[TD([[makeQuery(id+"F0.imprint","IMPRINT",EDGE,{"derivedFrom":sQuery(id+"F0.wireOp",EDGE,"E281.2.3.0")}),1.0]])]});
            var Q25;
            Q25=makeQuery(id+"F0.imprint","IMPRINT",FACE,{"disambiguationData":[TD([[makeQuery(id+"F0.imprint","IMPRINT",EDGE,{"derivedFrom":sQuery(id+"F0.wireOp",EDGE,"E281.1.3.0")}),1.0]])]});
            var Q26;
            Q26=makeQuery(id+"F0.imprint","IMPRINT",FACE,{"disambiguationData":[TD([[makeQuery(id+"F0.imprint","IMPRINT",EDGE,{"derivedFrom":sQuery(id+"F0.wireOp",EDGE,"E281.0.3.0")}),1.0]])]});
            extrude(context, id + "F15", {"entities" : qUnion([Q0, Q1, Q2, Q3, Q4, Q5, Q6, Q7, Q8, Q9, Q10, Q11, Q12, Q13, Q14, Q15, Q16, Q17, Q18, Q19, Q20, Q21, Q22, Q23, Q24, Q25, Q26]), "depth" : 3 * mm, "offsetDistance" : 25 * mm});
        }
    });
